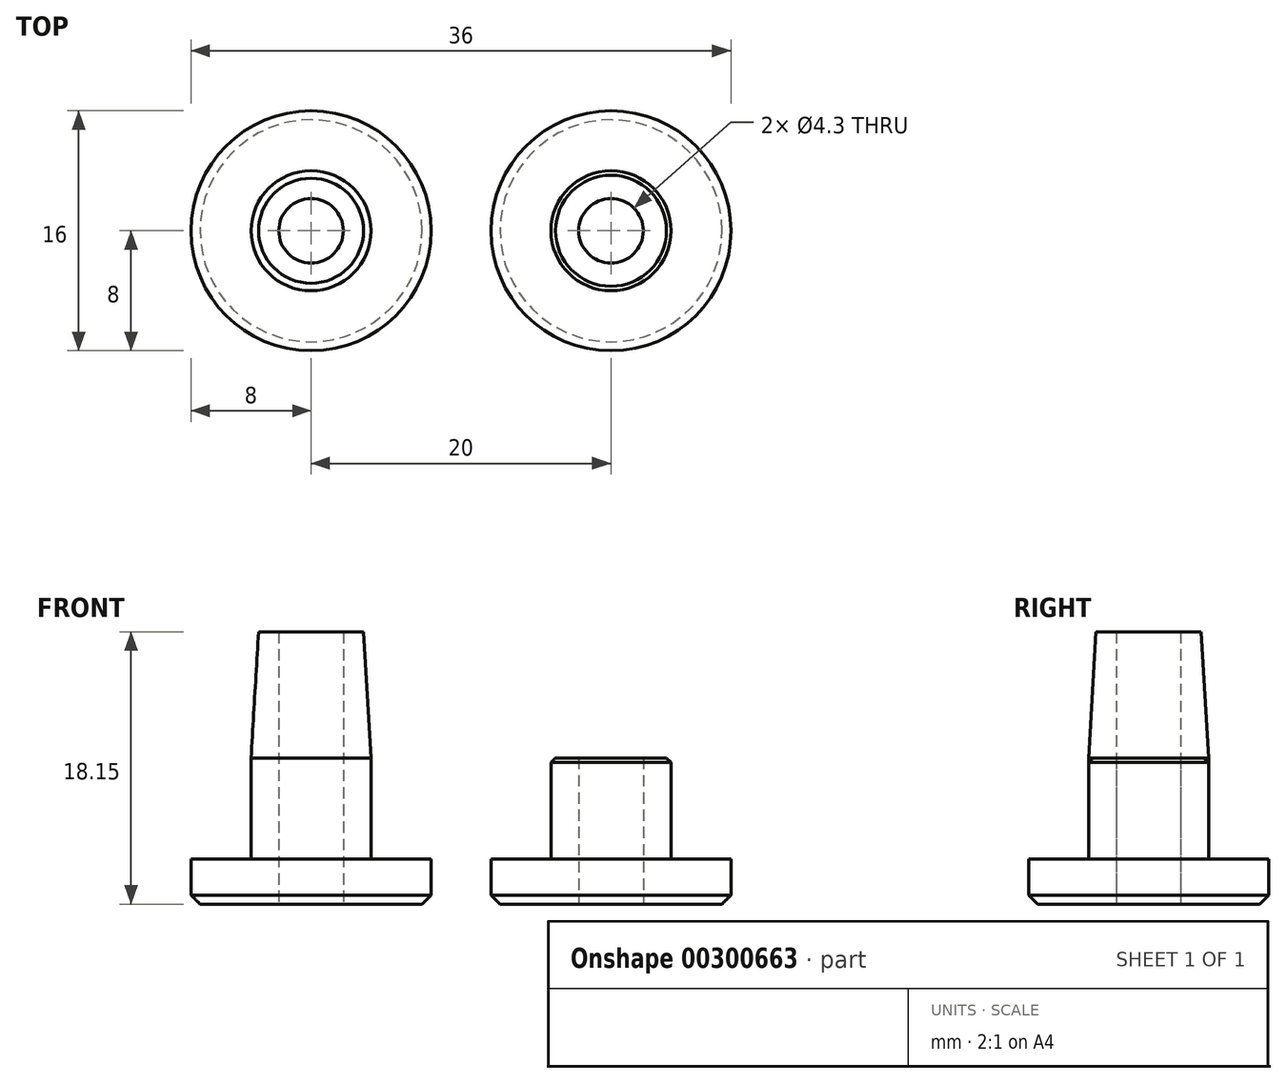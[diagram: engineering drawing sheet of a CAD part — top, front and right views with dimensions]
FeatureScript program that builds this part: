
annotation { "Feature Type Name" : "Feature", "Feature Type Description" : "" }
export const myFeature = defineFeature(function(context is Context, id is Id, definition is map)
    precondition{}
    {
        {
            var Q0;
            Q0=qCreatedBy(makeId("Front.planeOp"),FACE);
            var sketch = newSketch(context, id + "F0", { "sketchPlane" : qUnion([Q0])});
            skLineSegment(sketch, "E0", {"start": v(-4, 9.75) * mm, "end": v(-4, 3) * mm});
            skLineSegment(sketch, "E1", {"start": v(-4, 3) * mm, "end": v(-8, 3) * mm});
            skLineSegment(sketch, "E2", {"start": v(-8, 3) * mm, "end": v(-8, 0) * mm});
            skLineSegment(sketch, "E3", {"start": v(-4, 9.75) * mm, "end": v(-3.5, 18.15) * mm});
            skLineSegment(sketch, "E4", {"start": v(0, 0) * mm, "end": v(0, 19.23) * mm, "construction": true});
            skLineSegment(sketch, "E5", {"start": v(-3.5, 18.15) * mm, "end": v(0, 18.15) * mm});
            skLineSegment(sketch, "E6", {"start": v(0, 18.15) * mm, "end": v(0, 0) * mm});
            skLineSegment(sketch, "E7", {"start": v(0, 0) * mm, "end": v(-8, 0) * mm});
            skLineSegment(sketch, "E8", {"start": v(12, 0) * mm, "end": v(20, 0) * mm});
            skLineSegment(sketch, "E9", {"start": v(20, 0) * mm, "end": v(20, 9.75) * mm});
            skLineSegment(sketch, "E10", {"start": v(20, 9.75) * mm, "end": v(16, 9.75) * mm});
            skLineSegment(sketch, "E11", {"start": v(16, 9.75) * mm, "end": v(16, 3) * mm});
            skLineSegment(sketch, "E12", {"start": v(16, 3) * mm, "end": v(12, 3) * mm});
            skLineSegment(sketch, "E13", {"start": v(12, 3) * mm, "end": v(12, 0) * mm});
            skSolve(sketch);
        }
        {
            var Q0;
            Q0=makeQuery(id+"F0.imprint","IMPRINT",FACE,{"disambiguationData":[TD([[makeQuery(id+"F0.imprint","IMPRINT",EDGE,{"derivedFrom":sQuery(id+"F0.wireOp",EDGE,"E0")}),1.0]])]});
            var Q1;
            Q1=sQuery(id+"F0.wireOp",EDGE,"E4");
            revolve(context, id + "F1", {"entities" : qUnion([Q0]), "axis" : qUnion([Q1]), "revolveType" : RevolveType.FULL});
        }
        {
            var Q0;
            Q0=makeQuery(id+"F0.imprint","IMPRINT",FACE,{"disambiguationData":[TD([[makeQuery(id+"F0.imprint","IMPRINT",EDGE,{"derivedFrom":sQuery(id+"F0.wireOp",EDGE,"E8")}),1.0]])]});
            var Q1;
            Q1=sQuery(id+"F0.wireOp",EDGE,"E9");
            revolve(context, id + "F2", {"entities" : qUnion([Q0]), "axis" : qUnion([Q1]), "revolveType" : RevolveType.FULL});
        }
        {
            var Q0;
            Q0=qCreatedBy(makeId("Top.planeOp"),FACE);
            var sketch = newSketch(context, id + "F3", { "sketchPlane" : qUnion([Q0])});
            skCircle(sketch, "E14", {"center": v(0, 0) * mm, "radius": 2.15 * mm});
            skCircle(sketch, "E15", {"center": v(20, 0) * mm, "radius": 2.15 * mm});
            skSolve(sketch);
        }
        {
            var Q0;
            Q0 = qSketchRegion(id + "F3", true);
            extrude(context, id + "F4", {"entities" : qUnion([Q0]), "operationType" : NewBodyOperationType.REMOVE, "endBound" : BoundingType.THROUGH_ALL, "depth" : 25 * mm});
        }
        {
            var Q0;
            Q0=makeQuery(id+"F1.opRevolve","SWEPT_EDGE",EDGE,{"disambiguationData":[OSD([sQuery(id+"F0.wireOp",EDGE,"E2"),sQuery(id+"F0.wireOp",EDGE,"E7")])]});
            var Q1;
            Q1=makeQuery(id+"F2.opRevolve","SWEPT_EDGE",EDGE,{"disambiguationData":[OSD([sQuery(id+"F0.wireOp",EDGE,"E8"),sQuery(id+"F0.wireOp",EDGE,"E13")])]});
            chamfer(context, id + "F5", {"entities" : qUnion([Q0, Q1]), "width" : .6 * mm, "tangentPropagation" : true});
        }
        {
            var Q0;
            Q0=makeQuery(id+"F2.opRevolve","SWEPT_EDGE",EDGE,{"disambiguationData":[OSD([sQuery(id+"F0.wireOp",EDGE,"E10"),sQuery(id+"F0.wireOp",EDGE,"E11")])]});
            chamfer(context, id + "F6", {"entities" : qUnion([Q0]), "width" : .3 * mm, "tangentPropagation" : true});
        }
    });
